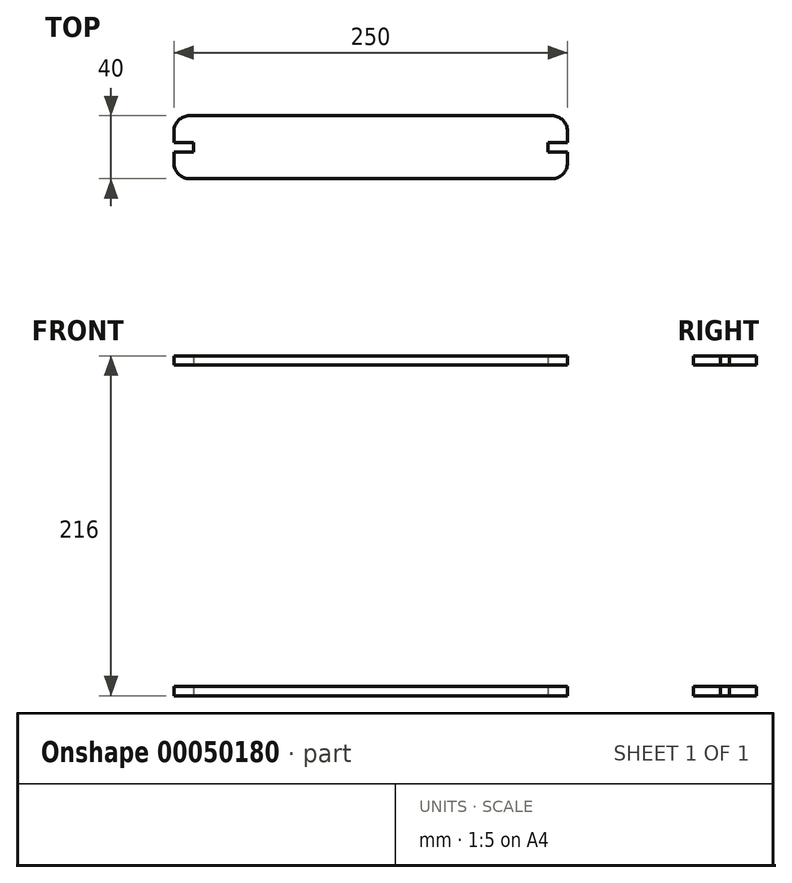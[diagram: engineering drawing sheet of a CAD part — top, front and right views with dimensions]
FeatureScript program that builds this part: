
annotation { "Feature Type Name" : "Feature", "Feature Type Description" : "" }
export const myFeature = defineFeature(function(context is Context, id is Id, definition is map)
    precondition{}
    {
        {
            var Q0;
            Q0=qCreatedBy(makeId("Top.planeOp"),FACE);
            var sketch = newSketch(context, id + "F0", { "sketchPlane" : qUnion([Q0])});
            skLineSegment(sketch, "E0.bottom", {"start": v(10, 0) * mm, "end": v(240, 0) * mm});
            skLineSegment(sketch, "E0.top", {"start": v(10, 40) * mm, "end": v(240, 40) * mm});
            skLineSegment(sketch, "E0.left", {"start": v(0, 10) * mm, "end": v(0, 17) * mm});
            skLineSegment(sketch, "E0.right", {"start": v(250, 10) * mm, "end": v(250, 17) * mm});
            skLineSegment(sketch, "E1", {"start": v(0, 23) * mm, "end": v(12.5, 23) * mm});
            skLineSegment(sketch, "E2", {"start": v(12.5, 23) * mm, "end": v(12.5, 17) * mm});
            skLineSegment(sketch, "E3", {"start": v(12.5, 17) * mm, "end": v(0, 17) * mm});
            skLineSegment(sketch, "E4", {"start": v(250, 23) * mm, "end": v(237.5, 23) * mm});
            skLineSegment(sketch, "E5", {"start": v(237.5, 23) * mm, "end": v(237.5, 17) * mm});
            skLineSegment(sketch, "E6", {"start": v(237.5, 17) * mm, "end": v(250, 17) * mm});
            skLineSegment(sketch, "E7.trimOffspring", {"start": v(250, 23) * mm, "end": v(250, 30) * mm});
            skLineSegment(sketch, "E8.trimOffspring", {"start": v(0, 23) * mm, "end": v(0, 30) * mm});
            skPoint(sketch, "E9.visualSharp", {"position": v(0, 40) * mm});
            skArc(sketch, "E9.filletArc", {"start": v(10, 40) * mm, "mid": v(2.93, 37.07) * mm, "end": v(0, 30) * mm});
            skPoint(sketch, "E10.visualSharp", {"position": v(0, 0) * mm});
            skArc(sketch, "E10.filletArc", {"start": v(0, 10) * mm, "mid": v(2.93, 2.93) * mm, "end": v(10, 0) * mm});
            skPoint(sketch, "E11.visualSharp", {"position": v(250, 40) * mm});
            skArc(sketch, "E11.filletArc", {"start": v(250, 30) * mm, "mid": v(247.07, 37.07) * mm, "end": v(240, 40) * mm});
            skPoint(sketch, "E12.visualSharp", {"position": v(250, 0) * mm});
            skArc(sketch, "E12.filletArc", {"start": v(240, 0) * mm, "mid": v(247.07, 2.93) * mm, "end": v(250, 10) * mm});
            skSolve(sketch);
        }
        {
            var Q0;
            Q0 = qSketchRegion(id + "F0", true);
            extrude(context, id + "F1", {"entities" : qUnion([Q0]), "depth" : 6 * mm});
        }
        {
            var Q0;
            Q0=makeQuery(id+"F1.opExtrude","SWEPT_BODY",BODY,{"disambiguationData":[OSD([sQuery(id+"F0.wireOp",EDGE,"E0.bottom"),sQuery(id+"F0.wireOp",EDGE,"E0.top"),sQuery(id+"F0.wireOp",EDGE,"E0.left"),sQuery(id+"F0.wireOp",EDGE,"E0.right"),sQuery(id+"F0.wireOp",EDGE,"E1"),sQuery(id+"F0.wireOp",EDGE,"E2"),sQuery(id+"F0.wireOp",EDGE,"E3"),sQuery(id+"F0.wireOp",EDGE,"E4"),sQuery(id+"F0.wireOp",EDGE,"E5"),sQuery(id+"F0.wireOp",EDGE,"E6"),sQuery(id+"F0.wireOp",EDGE,"E7.trimOffspring"),sQuery(id+"F0.wireOp",EDGE,"E8.trimOffspring"),sQuery(id+"F0.wireOp",EDGE,"E9.filletArc"),sQuery(id+"F0.wireOp",EDGE,"E10.filletArc"),sQuery(id+"F0.wireOp",EDGE,"E11.filletArc"),sQuery(id+"F0.wireOp",EDGE,"E12.filletArc")])]});
            transform(context, id + "F2", {"entities" : qUnion([Q0]), "transformType" : TransformType.TRANSLATION_3D, "dx" : 0 * mm, "dy" : 0 * mm, "dz" : 210 * mm, "makeCopy" : true});
        }
        {
            var Q0;
            Q0=makeQuery(id+"F1.opExtrude","CAP_VERTEX",VERTEX,{"disambiguationData":[OSD([sQuery(id+"F0.wireOp",EDGE,"E0.right"),sQuery(id+"F0.wireOp",EDGE,"E6")])],"isStart":true});
            var Q1;
            Q1=makeQuery(id+"F2.opPattern","COPY",VERTEX,{"derivedFrom":makeQuery(id+"F1.opExtrude","CAP_VERTEX",VERTEX,{"disambiguationData":[OSD([sQuery(id+"F0.wireOp",EDGE,"E0.right"),sQuery(id+"F0.wireOp",EDGE,"E6")])],"isStart":false}),"instanceName":"1"});
            var Q2;
            Q2=makeQuery(id+"F2.opPattern","COPY",VERTEX,{"derivedFrom":makeQuery(id+"F1.opExtrude","CAP_VERTEX",VERTEX,{"disambiguationData":[OSD([sQuery(id+"F0.wireOp",EDGE,"E0.left"),sQuery(id+"F0.wireOp",EDGE,"E3")])],"isStart":false}),"instanceName":"1"});
            cPlane(context, id + "F3", {"entities" : qUnion([Q0, Q1, Q2]), "cplaneType" : CPlaneType.THREE_POINT, "offset" : 10 * mm, "width" : 150 * mm, "height" : 150 * mm});
        }
    });
